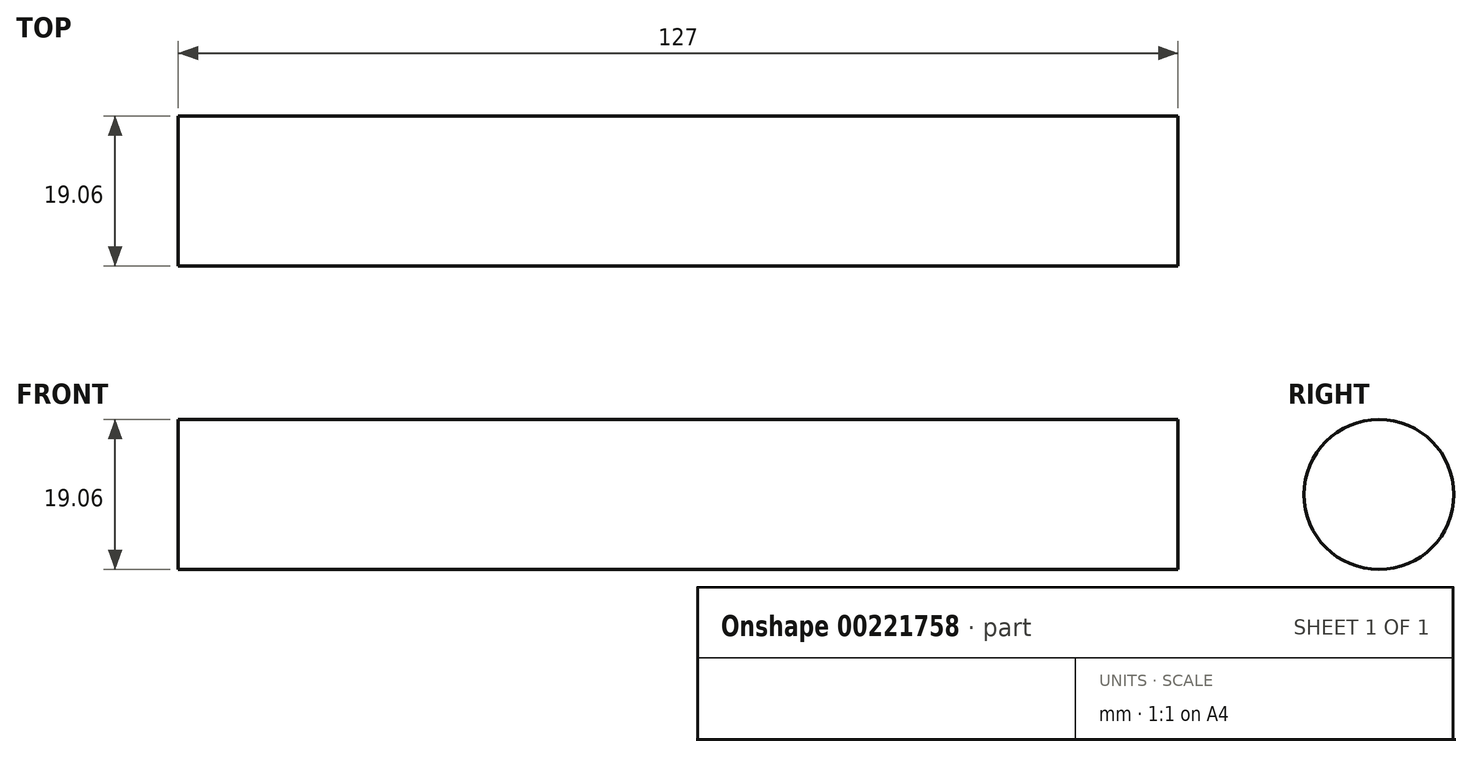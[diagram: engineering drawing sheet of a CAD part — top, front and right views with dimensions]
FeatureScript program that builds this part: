
annotation { "Feature Type Name" : "Feature", "Feature Type Description" : "" }
export const myFeature = defineFeature(function(context is Context, id is Id, definition is map)
    precondition{}
    {
        {
            var Q0;
            Q0=qCreatedBy(makeId("Right.planeOp"),FACE);
            var sketch = newSketch(context, id + "F0", { "sketchPlane" : qUnion([Q0])});
            skCircle(sketch, "E0", {"center": v(0, 0) * mm, "radius": 9.53 * mm});
            skSolve(sketch);
        }
        {
            var Q0;
            Q0 = qSketchRegion(id + "F0", true);
            extrude(context, id + "F1", {"entities" : qUnion([Q0]), "oppositeDirection" : true, "depth" : 127 * mm});
        }
    });
